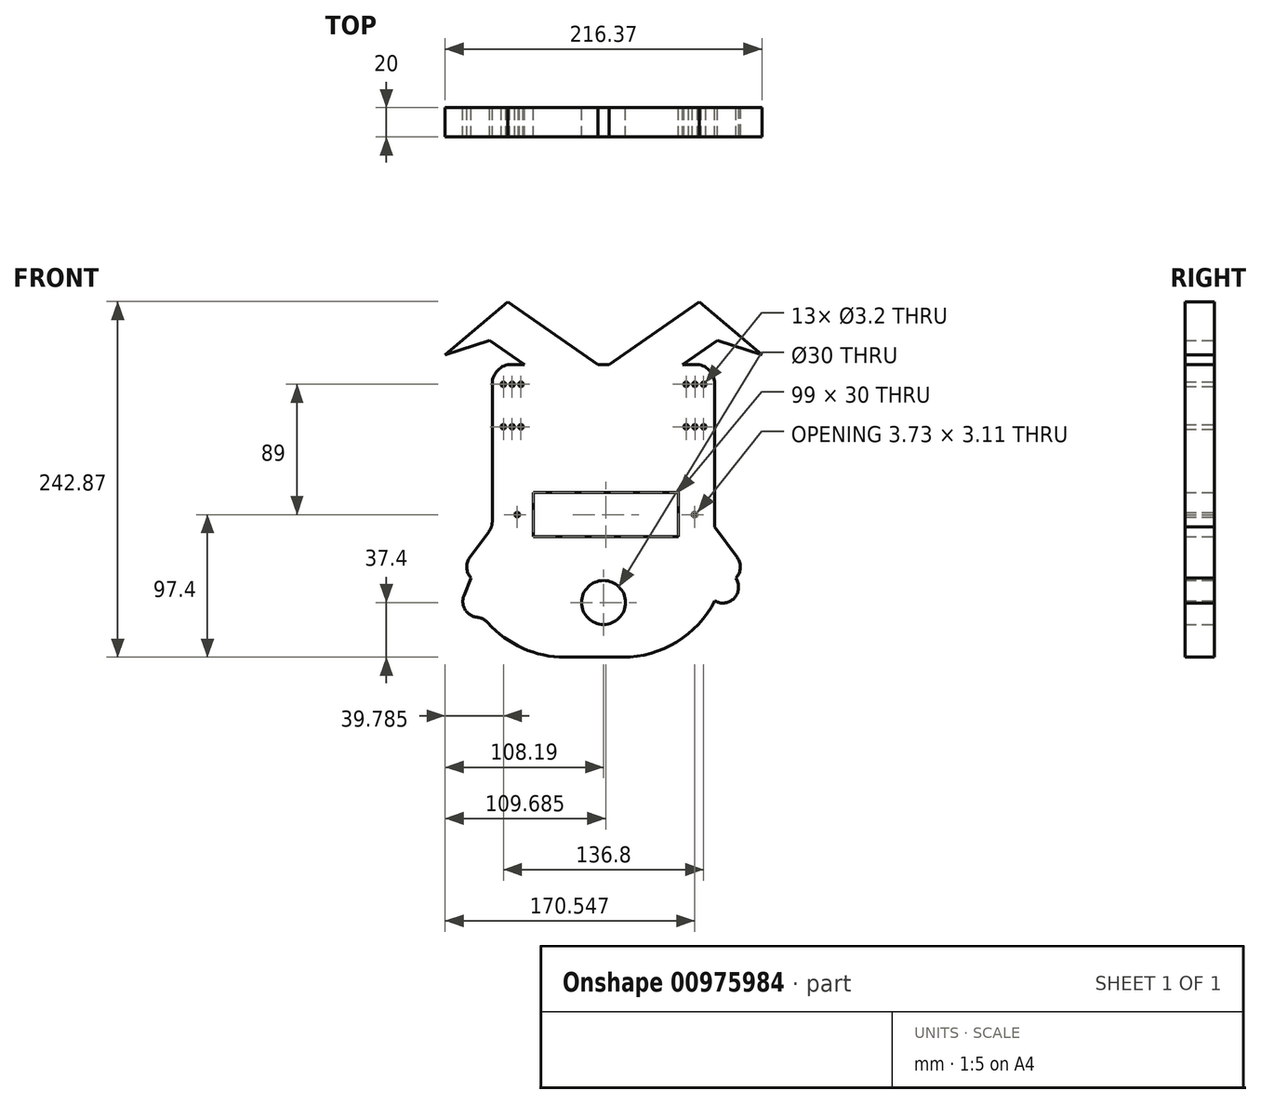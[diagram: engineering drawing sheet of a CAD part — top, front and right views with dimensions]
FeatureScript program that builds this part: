
annotation { "Feature Type Name" : "Feature", "Feature Type Description" : "" }
export const myFeature = defineFeature(function(context is Context, id is Id, definition is map)
    precondition{}
    {
        {
            var Q0;
            Q0=qCreatedBy(makeId("Front.planeOp"),FACE);
            var sketch = newSketch(context, id + "F0", { "sketchPlane" : qUnion([Q0])});
            skLineSegment(sketch, "E0.bottom", {"start": v(-76, 102.6) * mm, "end": v(76, 102.6) * mm});
            skLineSegment(sketch, "E0.top", {"start": v(-76, -97.4) * mm, "end": v(76, -97.4) * mm});
            skLineSegment(sketch, "E0.left", {"start": v(-76, 102.6) * mm, "end": v(-76, -97.4) * mm});
            skLineSegment(sketch, "E0.right", {"start": v(76, 102.6) * mm, "end": v(76, -97.4) * mm});
            skCircle(sketch, "E1", {"center": v(0, -60) * mm, "radius": 15 * mm});
            skLineSegment(sketch, "E2.bottom", {"start": v(-48, 15) * mm, "end": v(51, 15) * mm});
            skLineSegment(sketch, "E2.top", {"start": v(-48, -15) * mm, "end": v(51, -15) * mm});
            skLineSegment(sketch, "E2.left", {"start": v(-48, 15) * mm, "end": v(-48, -15) * mm});
            skLineSegment(sketch, "E2.right", {"start": v(51, 15) * mm, "end": v(51, -15) * mm});
            skCircle(sketch, "E3", {"center": v(-68.4, 60) * mm, "radius": 1.6 * mm});
            skCircle(sketch, "E4.0.1.0", {"center": v(-68.4, 89) * mm, "radius": 1.6 * mm});
            skCircle(sketch, "E4.1.0.0", {"center": v(-62.4, 60) * mm, "radius": 1.6 * mm});
            skCircle(sketch, "E4.1.1.0", {"center": v(-62.4, 89) * mm, "radius": 1.6 * mm});
            skCircle(sketch, "E4.2.0.0", {"center": v(-56.4, 60) * mm, "radius": 1.6 * mm});
            skCircle(sketch, "E4.2.1.0", {"center": v(-56.4, 89) * mm, "radius": 1.6 * mm});
            skLineSegment(sketch, "E4.direction1", {"start": v(-68.4, 60) * mm, "end": v(-62.4, 60) * mm, "construction": true});
            skLineSegment(sketch, "E4.direction2", {"start": v(-68.4, 60) * mm, "end": v(-68.4, 89) * mm, "construction": true});
            skLineSegment(sketch, "E5", {"start": v(-76, 102.6) * mm, "end": v(0, 102.6) * mm});
            skLineSegment(sketch, "E6", {"start": v(0, 102.6) * mm, "end": v(0, 2.6) * mm});
            skCircle(sketch, "E7.MirrorC", {"center": v(56.4, 60) * mm, "radius": 1.6 * mm});
            skCircle(sketch, "E8.MirrorC", {"center": v(56.4, 89) * mm, "radius": 1.6 * mm});
            skCircle(sketch, "E9.MirrorC", {"center": v(62.4, 89) * mm, "radius": 1.6 * mm});
            skCircle(sketch, "E10.MirrorC", {"center": v(62.4, 60) * mm, "radius": 1.6 * mm});
            skCircle(sketch, "E11.MirrorC", {"center": v(68.4, 60) * mm, "radius": 1.6 * mm});
            skCircle(sketch, "E12.MirrorC", {"center": v(68.4, 89) * mm, "radius": 1.6 * mm});
            skCircle(sketch, "E13", {"center": v(62.1, 0) * mm, "radius": 1.6 * mm});
            skLineSegment(sketch, "E14", {"start": v(51, -15) * mm, "end": v(64.22, 0) * mm});
            skLineSegment(sketch, "E15", {"start": v(64.22, 0) * mm, "end": v(51, 15) * mm});
            skLineSegment(sketch, "E16", {"start": v(-48, -15) * mm, "end": v(-61.23, 0) * mm});
            skLineSegment(sketch, "E17", {"start": v(-61.23, 0) * mm, "end": v(-61.23, 0) * mm});
            skLineSegment(sketch, "E18", {"start": v(-61.23, 0) * mm, "end": v(-48, 15) * mm});
            skLineSegment(sketch, "E19", {"start": v(76, -58.92) * mm, "end": v(105, -79.88) * mm});
            skLineSegment(sketch, "E20", {"start": v(105, -79.88) * mm, "end": v(105, -79.88) * mm});
            skLineSegment(sketch, "E21", {"start": v(105, -79.88) * mm, "end": v(90.5, -43.2) * mm});
            skLineSegment(sketch, "E22", {"start": v(90.5, -43.2) * mm, "end": v(103.12, -45.43) * mm});
            skLineSegment(sketch, "E23", {"start": v(103.12, -45.43) * mm, "end": v(103.12, -45.43) * mm});
            skLineSegment(sketch, "E24", {"start": v(103.12, -45.43) * mm, "end": v(76, -8.45) * mm});
            skLineSegment(sketch, "E25", {"start": v(76, -8.45) * mm, "end": v(76, -8.45) * mm});
            skLineSegment(sketch, "E26.MirrorCS", {"start": v(-103.14, -45.43) * mm, "end": v(-76, -8.45) * mm});
            skLineSegment(sketch, "E27.MirrorCS", {"start": v(-90.51, -43.2) * mm, "end": v(-103.14, -45.43) * mm});
            skLineSegment(sketch, "E28.MirrorCS", {"start": v(-105.02, -79.88) * mm, "end": v(-90.51, -43.2) * mm});
            skLineSegment(sketch, "E29.MirrorCS", {"start": v(-76, -58.92) * mm, "end": v(-105.02, -79.88) * mm});
            skCircle(sketch, "E30", {"center": v(-58.93, 0) * mm, "radius": 1.6 * mm});
            skLineSegment(sketch, "E31", {"start": v(-54.1, 102.6) * mm, "end": v(-77.67, 119) * mm});
            skLineSegment(sketch, "E32", {"start": v(-77.67, 119) * mm, "end": v(-77.67, 119) * mm});
            skLineSegment(sketch, "E33", {"start": v(-77.67, 119) * mm, "end": v(-108.19, 109.17) * mm});
            skLineSegment(sketch, "E34", {"start": v(-108.19, 109.17) * mm, "end": v(-65.41, 145.47) * mm});
            skLineSegment(sketch, "E35", {"start": v(-65.41, 145.47) * mm, "end": v(-65.41, 145.47) * mm});
            skLineSegment(sketch, "E36", {"start": v(-65.41, 145.47) * mm, "end": v(-1.7, 101.14) * mm});
            skLineSegment(sketch, "E37.MirrorCS", {"start": v(65.4, 145.47) * mm, "end": v(1.69, 101.14) * mm});
            skLineSegment(sketch, "E38.MirrorCS", {"start": v(77.66, 119) * mm, "end": v(108.18, 109.17) * mm});
            skLineSegment(sketch, "E39.MirrorCS", {"start": v(54.1, 102.6) * mm, "end": v(77.66, 119) * mm});
            skLineSegment(sketch, "E40.MirrorCS", {"start": v(108.18, 109.17) * mm, "end": v(65.4, 145.47) * mm});
            skPoint(sketch, "E41.center.orphan", {"position": v(-64.69, 0) * mm});
            skSolve(sketch);
        }
        {
            var Q0;
            Q0=qSketchRegion(id+"F0",true);
            var Q1;
            Q1=makeQuery(id+"F0.imprint","IMPRINT",FACE,{"disambiguationData":[TD([[makeQuery(id+"F0.imprint","IMPRINT",EDGE,{"derivedFrom":sQuery(id+"F0.wireOp",EDGE,"E0.bottom")}),-1.0]])]});
            var Q2;
            {var subQ0=sQuery(id+"F0.wireOp",EDGE,"E2.right");Q2=makeQuery(id+"F0.imprint","IMPRINT",FACE,{"disambiguationData":[TD([[makeQuery(id+"F0.imprint","IMPRINT",EDGE,{"derivedFrom":subQ0}),1.0]])]});}
            var Q3;
            Q3=makeQuery(id+"F0.imprint","IMPRINT",FACE,{"disambiguationData":[TD([[makeQuery(id+"F0.imprint","IMPRINT",EDGE,{"derivedFrom":sQuery(id+"F0.wireOp",EDGE,"E2.left")}),-1.0]])]});
            extrude(context, id + "F1", {"entities" : qUnion([Q0, Q1, Q2, Q3]), "depth" : 20 * mm, "offsetDistance" : 25 * mm});
        }
        {
            var Q0;
            Q0=makeQuery(id+"F1.opExtrude","SWEPT_EDGE",EDGE,{"disambiguationData":[OSD([sQuery(id+"F0.wireOp",EDGE,"E0.left"),sQuery(id+"F0.wireOp",EDGE,"E5")])]});
            var Q1;
            Q1=makeQuery(id+"F1.opExtrude","SWEPT_EDGE",EDGE,{"disambiguationData":[OSD([sQuery(id+"F0.wireOp",EDGE,"E0.top"),sQuery(id+"F0.wireOp",EDGE,"E0.left")])]});
            var Q2;
            Q2=makeQuery(id+"F1.opExtrude","SWEPT_EDGE",EDGE,{"disambiguationData":[OSD([sQuery(id+"F0.wireOp",EDGE,"E0.top"),sQuery(id+"F0.wireOp",EDGE,"E0.right")])]});
            var Q3;
            Q3=makeQuery(id+"F1.opExtrude","SWEPT_EDGE",EDGE,{"disambiguationData":[OSD([sQuery(id+"F0.wireOp",EDGE,"E0.bottom"),sQuery(id+"F0.wireOp",EDGE,"E0.right")])]});
            fillet(context, id + "F2", {"entities" : qUnion([Q0, Q1, Q2, Q3]), "radius" : 11.6 * mm, "tangentPropagation" : true, "allowEdgeOverflow" : false});
        }
        {
            var Q0;
            Q0=qSketchRegion(id+"F0",true);
            var Q1;
            Q1=makeQuery(id+"F0.imprint","IMPRINT",FACE,{"disambiguationData":[TD([[makeQuery(id+"F0.imprint","IMPRINT",EDGE,{"derivedFrom":sQuery(id+"F0.wireOp",EDGE,"E0.bottom")}),-1.0]])]});
            var Q2;
            Q2=makeQuery(id+"F0.imprint","IMPRINT",FACE,{"disambiguationData":[TD([[makeQuery(id+"F0.imprint","IMPRINT",EDGE,{"derivedFrom":sQuery(id+"F0.wireOp",EDGE,"E2.left")}),-1.0]])]});
            var Q3;
            {var subQ0=sQuery(id+"F0.wireOp",EDGE,"E2.right");Q3=makeQuery(id+"F0.imprint","IMPRINT",FACE,{"disambiguationData":[TD([[makeQuery(id+"F0.imprint","IMPRINT",EDGE,{"derivedFrom":subQ0}),1.0]])]});}
            extrude(context, id + "F3", {"entities" : qUnion([Q0, Q1, Q2, Q3]), "operationType" : NewBodyOperationType.ADD, "depth" : 20 * mm, "offsetDistance" : 25 * mm});
        }
        {
            var Q0;
            Q0=makeQuery(id+"F3.opExtrude","SWEPT_EDGE",EDGE,{"disambiguationData":[OSD([sQuery(id+"F0.wireOp",EDGE,"E0.top"),sQuery(id+"F0.wireOp",EDGE,"E0.left")])]});
            var Q1;
            Q1=makeQuery(id+"F3.opExtrude","SWEPT_EDGE",EDGE,{"disambiguationData":[OSD([sQuery(id+"F0.wireOp",EDGE,"E0.top"),sQuery(id+"F0.wireOp",EDGE,"E0.right")])]});
            fillet(context, id + "F4", {"entities" : qUnion([Q0, Q1]), "radius" : 70.72 * mm, "tangentPropagation" : true, "allowEdgeOverflow" : false});
        }
        {
            var Q0;
            Q0=makeQuery(id+"F0.imprint","IMPRINT",FACE,{"disambiguationData":[TD([[makeQuery(id+"F0.imprint","IMPRINT",EDGE,{"derivedFrom":sQuery(id+"F0.wireOp",EDGE,"E0.bottom")}),-1.0]])]});
            var sketch = newSketch(context, id + "F5", { "sketchPlane" : qUnion([Q0])});
            skSolve(sketch);
        }
        {
            var Q0;
            Q0=makeQuery(id+"F3.opExtrude","SWEPT_EDGE",EDGE,{"disambiguationData":[OSD([sQuery(id+"F0.wireOp",EDGE,"E0.bottom"),sQuery(id+"F0.wireOp",EDGE,"E0.right")])]});
            var Q1;
            Q1=makeQuery(id+"F3.opExtrude","SWEPT_EDGE",EDGE,{"disambiguationData":[OSD([sQuery(id+"F0.wireOp",EDGE,"E0.left"),sQuery(id+"F0.wireOp",EDGE,"E5")])]});
            fillet(context, id + "F6", {"entities" : qUnion([Q0, Q1]), "radius" : 13.12 * mm, "tangentPropagation" : true, "allowEdgeOverflow" : false});
        }
        {
            var Q0;
            Q0=makeQuery(id+"F1.opExtrude","SWEPT_EDGE",EDGE,{"disambiguationData":[OSD([sQuery(id+"F0.wireOp",EDGE,"E22"),sQuery(id+"F0.wireOp",EDGE,"E24")])]});
            var Q1;
            Q1=makeQuery(id+"F1.opExtrude","SWEPT_EDGE",EDGE,{"disambiguationData":[OSD([sQuery(id+"F0.wireOp",EDGE,"E28.MirrorCS"),sQuery(id+"F0.wireOp",EDGE,"E29.MirrorCS")])]});
            var Q2;
            Q2=makeQuery(id+"F1.opExtrude","SWEPT_EDGE",EDGE,{"disambiguationData":[OSD([sQuery(id+"F0.wireOp",EDGE,"E26.MirrorCS"),sQuery(id+"F0.wireOp",EDGE,"E27.MirrorCS")])]});
            var Q3;
            Q3=makeQuery(id+"F1.opExtrude","SWEPT_EDGE",EDGE,{"disambiguationData":[OSD([sQuery(id+"F0.wireOp",EDGE,"E19"),sQuery(id+"F0.wireOp",EDGE,"E21")])]});
            fillet(context, id + "F7", {"entities" : qUnion([Q0, Q1, Q2, Q3]), "radius" : 10.79 * mm, "tangentPropagation" : true, "allowEdgeOverflow" : false});
        }
    });
